# Revit family: Hager-Volta-IP30-Surface_mounted-pusty-NoHosted-PL-pl
name_source: partatom
category: Electrical Equipment
units: mm (PartAtom-declared; Revit-internal decimal feet)

## family parameters
Always vertical = Yes
Cut with Voids When Loaded = No
Panel Configuration = Two Columns, Circuits Across
Part Type = Panelboard
Room Calculation Point = No
Round Connector Dimension = Use Diameter
Shared = No
Work Plane-Based = Yes

## types (4) — shared parameters
Default Elevation = 1219 mm
EF000003 - Sposób montażu = EV000384 - Montaż natynkowy
EF000008 - Szerokość = 305 mm  [stored 1.00066 ft]
EF000049 - Głębokość = 96 mm  [stored 0.314961 ft]
EF000116 - Numer RAL = 9010
EF000118 - Z płytą montażową = Yes
EF001062 - Wykonane zgodnie z Dyrektywą Kompatybilności Elektromagnetycznej EMC = No
EF002950 - Szerokość wyrażona liczbą modułów = 12
EF005474 - Stopień ochrony (IP) = EV006410 - IP30
EF006244 - Transparentna pokrywa/drzwi = No
EF006306 - Z zamkiem = No
EF015776 - Listwa zaciskowa uziemienia = No
EF015777 - Listwa zaciskowa przewodu neutralnego = No
EF015941 - Drzwi przepuszczające sygnał = No
HG000002 - Z drzwiami lub pokrywą = Yes
HG000003 - Zakres = Volta
HG000005 - Grubość = 3 mm  [stored 0.00984252 ft]
HG000006 - Montaż podtynkowy = No
HG000009 - Drzwi dwuskrzydłowe = No
HG000010 - Drzwi asymetryczne = No
HG000011 - Puste rzędy od dołu = No
HG000017 - Odległość między biegunami = 18 mm  [stored 0.0590551 ft]
Manufacturer = Hager
Type Comments = Volta
zero-valued in all types: EF000218 - Głębokość wbudowania, EF000332 - Wysokość wbudowania, EF000846 - Szerokość wbudowania, HG000001 - Liczba kolumn, HG000007 - Liczba pustych kolumn, HG000008 - Liczba pustych rzędów

## per-type parameters (varying)
| type | EF000007 - Kolor | EF000040 - Wysokość | EF000266 - Liczba rzędów | EF000339 - Rodzaj pokrywy | EF001088 - Możliwość rozbudowy | EF001131 - Głębokość wewnętrzna | EF001134 - Szyna DIN | EF001596 - Materiał obudowy | EF004462 - Rodzaj zamknięcia | EF009212 - Wykonanie pokrywy | HG000004 - Referencja producenta | Model |
| Montaż natynkowy IP30 S305 W515 G96.5 12 Jednostki dywizyjne - VA36NWB |  | 515 mm | 0 | EV004216 - Drzwi | Yes | 0 mm  [stored 0 ft] | No |  | EV000154 - Inne | EV009916 - Z otworem | VA36NWB | VA36NWB |
| Montaż natynkowy IP30 S305 W515 G96.5 12 Jednostki dywizyjne - VA36NWP | EV000202 - Biały | 515 mm | 3 | EV004216 - Drzwi | Yes | 92 mm | Yes | EV000154 - Inne | EV000154 - Inne | EV009916 - Z otworem | VA36NWP | VA36NWP |
| Montaż natynkowy IP30 S305 W640 G96.5 12 Jednostki dywizyjne - VA48NWB |  | 640 mm  [stored 2.09974 ft] | 0 | EV004216 - Drzwi | Yes | 0 mm  [stored 0 ft] | No |  | EV000154 - Inne | EV009916 - Z otworem | VA48NWB | VA48NWB |
| Montaż natynkowy IP30 S305 W640 G96.5 12 Jednostki dywizyjne - VA48NWP |  | 640 mm  [stored 2.09974 ft] | 0 |  | No | 0 mm  [stored 0 ft] | No |  |  |  | VA48NWP | VA48NWP |

note: [stored X ft] marks values corroborated as IEEE doubles in the binary element streams (Revit-internal decimal feet)

## geometry (parser evidence)
native form markers: Sweep x13
no freeform markers — native parametric forms only
